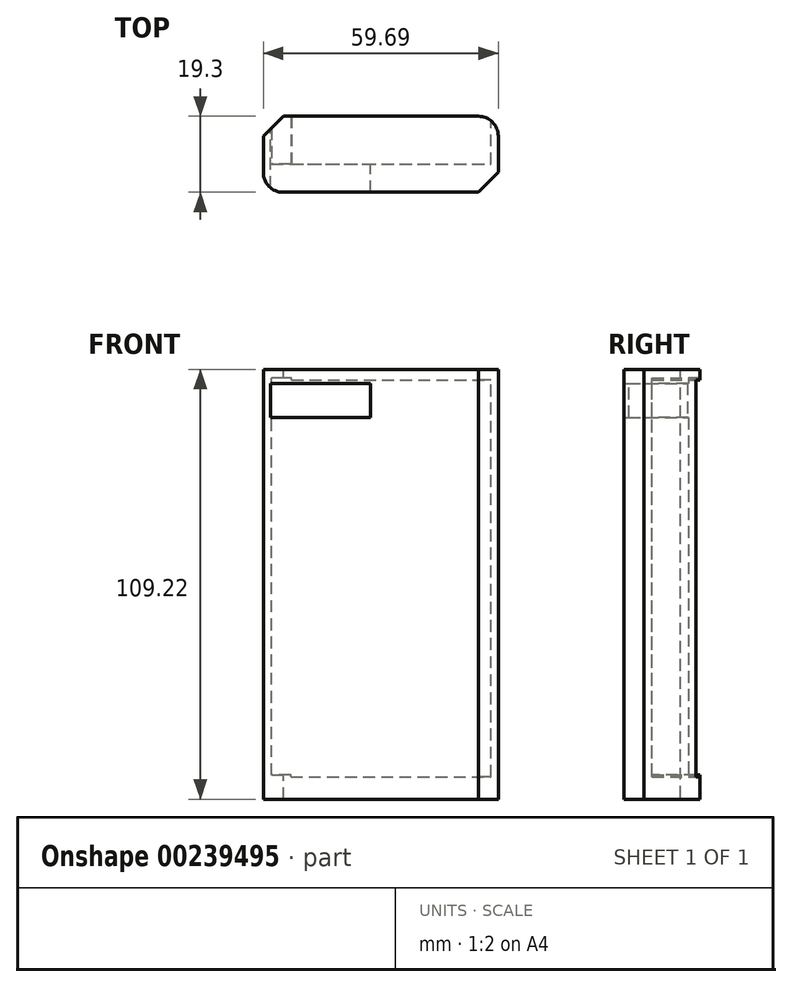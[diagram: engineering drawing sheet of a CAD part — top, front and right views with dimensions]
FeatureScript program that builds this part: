
annotation { "Feature Type Name" : "Feature", "Feature Type Description" : "" }
export const myFeature = defineFeature(function(context is Context, id is Id, definition is map)
    precondition{}
    {
        {
            var Q0;
            Q0=qCreatedBy(makeId("Front.planeOp"),FACE);
            var sketch = newSketch(context, id + "F0", { "sketchPlane" : qUnion([Q0])});
            skLineSegment(sketch, "E0.bottom", {"start": v(31.22, 54.61) * mm, "end": v(-28.47, 54.61) * mm});
            skLineSegment(sketch, "E0.top", {"start": v(31.22, -54.6) * mm, "end": v(-28.47, -54.61) * mm});
            skLineSegment(sketch, "E0.left", {"start": v(31.22, 54.61) * mm, "end": v(31.22, -54.6) * mm});
            skLineSegment(sketch, "E0.right", {"start": v(-28.47, 54.6) * mm, "end": v(-28.47, -54.61) * mm});
            skPoint(sketch, "E0.middle", {"position": v(1.38, 0) * mm});
            skSolve(sketch);
        }
        {
            var Q0;
            Q0 = qSketchRegion(id + "F0", true);
            extrude(context, id + "F1", {"entities" : qUnion([Q0]), "depth" : 19.3 * mm});
        }
        {
            var Q0;
            Q0=qCreatedBy(makeId("Front.planeOp"),FACE);
            var sketch = newSketch(context, id + "F2", { "sketchPlane" : qUnion([Q0])});
            skLineSegment(sketch, "E1.bottom", {"start": v(-21.48, -48.87) * mm, "end": v(29.32, -48.87) * mm});
            skLineSegment(sketch, "E1.top", {"start": v(-21.48, 51.96) * mm, "end": v(29.32, 51.96) * mm});
            skLineSegment(sketch, "E1.left", {"start": v(-21.48, -48.87) * mm, "end": v(-21.48, 51.96) * mm});
            skLineSegment(sketch, "E1.right", {"start": v(29.32, -48.87) * mm, "end": v(29.32, 51.96) * mm});
            skSolve(sketch);
        }
        {
            var Q0;
            Q0 = qSketchRegion(id + "F2", true);
            extrude(context, id + "F3", {"entities" : qUnion([Q0]), "operationType" : NewBodyOperationType.REMOVE, "depth" : 12.2 * mm});
        }
        {
            var Q0;
            Q0=qCreatedBy(makeId("Front.planeOp"),FACE);
            var sketch = newSketch(context, id + "F4", { "sketchPlane" : qUnion([Q0])});
            skLineSegment(sketch, "E2.bottom", {"start": v(-21.28, -48.48) * mm, "end": v(-26.4, -48.48) * mm});
            skLineSegment(sketch, "E2.top", {"start": v(-21.28, 52.36) * mm, "end": v(-26.4, 52.36) * mm});
            skLineSegment(sketch, "E2.left", {"start": v(-21.28, -48.48) * mm, "end": v(-21.28, 52.36) * mm});
            skLineSegment(sketch, "E2.right", {"start": v(-26.4, -48.48) * mm, "end": v(-26.4, 52.36) * mm});
            skSolve(sketch);
        }
        {
            var Q0;
            Q0 = qSketchRegion(id + "F4", true);
            extrude(context, id + "F5", {"entities" : qUnion([Q0]), "operationType" : NewBodyOperationType.REMOVE, "depth" : 12.2 * mm});
        }
        {
            var Q0;
            Q0=qCreatedBy(makeId("Front.planeOp"),FACE);
            var sketch = newSketch(context, id + "F6", { "sketchPlane" : qUnion([Q0])});
            skLineSegment(sketch, "E3.bottom", {"start": v(-13.2, 46.9) * mm, "end": v(-21.48, 46.9) * mm});
            skLineSegment(sketch, "E3.top", {"start": v(-13.2, 46.9) * mm, "end": v(-21.48, 46.9) * mm});
            skLineSegment(sketch, "E3.left", {"start": v(-13.2, 46.9) * mm, "end": v(-13.2, 46.9) * mm});
            skLineSegment(sketch, "E3.right", {"start": v(-21.48, 46.9) * mm, "end": v(-21.48, 46.9) * mm});
            skPoint(sketch, "E3.middle", {"position": v(-17.34, 46.9) * mm});
            skLineSegment(sketch, "E4.bottom", {"start": v(-1.2, 51.03) * mm, "end": v(-26.6, 51.03) * mm});
            skLineSegment(sketch, "E4.top", {"start": v(-1.2, 42.37) * mm, "end": v(-26.6, 42.37) * mm});
            skLineSegment(sketch, "E4.left", {"start": v(-1.2, 51.03) * mm, "end": v(-1.2, 42.37) * mm});
            skLineSegment(sketch, "E4.right", {"start": v(-26.6, 51.03) * mm, "end": v(-26.6, 42.37) * mm});
            skPoint(sketch, "E4.middle", {"position": v(-13.9, 46.7) * mm});
            skSolve(sketch);
        }
        {
            var Q0;
            Q0 = qSketchRegion(id + "F6", true);
            extrude(context, id + "F7", {"entities" : qUnion([Q0]), "operationType" : NewBodyOperationType.REMOVE, "depth" : 45.97 * mm});
        }
        {
            var Q0;
            Q0=makeQuery(id+"F1.opExtrude","CAP_EDGE",EDGE,{"disambiguationData":[OSD([sQuery(id+"F0.wireOp",EDGE,"E0.right")])],"isStart":false});
            fillet(context, id + "F8", {"entities" : qUnion([Q0]), "radius" : 5.08 * mm, "tangentPropagation" : true, "allowEdgeOverflow" : false});
        }
        {
            var Q0;
            Q0=makeQuery(id+"F1.opExtrude","CAP_EDGE",EDGE,{"disambiguationData":[OSD([sQuery(id+"F0.wireOp",EDGE,"E0.left")])],"isStart":false});
            chamfer(context, id + "F9", {"entities" : qUnion([Q0]), "width" : 5.08 * mm, "tangentPropagation" : true});
        }
        {
            var Q0;
            Q0=makeQuery(id+"F1.opExtrude","CAP_EDGE",EDGE,{"disambiguationData":[OSD([sQuery(id+"F0.wireOp",EDGE,"E0.left")])],"isStart":true});
            fillet(context, id + "F10", {"entities" : qUnion([Q0]), "radius" : 5.08 * mm, "tangentPropagation" : true, "allowEdgeOverflow" : false});
        }
        {
            var Q0;
            Q0=makeQuery(id+"F1.opExtrude","CAP_EDGE",EDGE,{"disambiguationData":[OSD([sQuery(id+"F0.wireOp",EDGE,"E0.right")])],"isStart":true});
            chamfer(context, id + "F11", {"entities" : qUnion([Q0]), "width" : 5.08 * mm, "tangentPropagation" : true});
        }
    });
